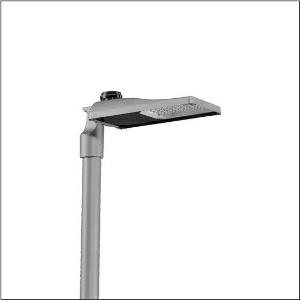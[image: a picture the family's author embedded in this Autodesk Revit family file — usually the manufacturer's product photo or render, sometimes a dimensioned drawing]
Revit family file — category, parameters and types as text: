
# Revit family: streetlight_sl_31_mini___st1_0a_5xh2d3bn08ha_f2e6
name_source: partatom
category: Lighting Fixtures
units: mm (PartAtom-declared; Revit-internal decimal feet)

## family parameters
Cut with Voids When Loaded = No
Host = Face
Light Source = No
Part Type = Normal
Room Calculation Point = No
Round Connector Dimension = Use Diameter
Shared = No

## types (1)
- --- (1 x LED, 9240 lm, 68.3 W, 3000K)
    Apparent Load = 68 VA
    CIE Flux Codes = 37 72 97 100 100
    Color Rendering = 70
    Color Temperature = 3000K
    Default Elevation = 1800 mm
    Description = Streetlight SL 31 mini NEMA (7pin) mast luminaire for post-top, side-entry; light control with lens of PMMA; light distribution: ST1.0a, direct asymmetric distribution, for standard-compliant lighting for roads and squares; LED: luminous flux: 9.240lm, light colour: 730, colour temperature: 3000K; luminous efficacy: 135,3lm/W; control: overheat protection, intelligent temperature release in ECG and LED module, constant luminous flux control, time-dependent luminous flux control, flexible luminous flux parameterisation, pre-setting: linear dimming characteristic; luminaire housing, of diecast aluminium, Siteco® metallic grey (DB 702S), corrosivity category C5 high according to DIN EN ISO 12944; cover of toughened safety glass, transparent, mast flange of diecast aluminium, Siteco® metallic grey (DB 702S), spigot size: 76/60mm, mast flange included unmounted; with cable H07RN-F 3x 1.5mm², cable length: 8,5m, connection cable pre-assembled; mains connection: 220..240V, AC, 50/60Hz; power consumption (at start of service life): 68,3W / (at end of service life): 74,8W / (with reduced operation 50%): 29,7W; protection rating (complete): IP66; insulation class (complete): insulation class I (protective earthing); impact resistance: IK10; certification: CE, ENEC, ENEC+, VDE, UKCA; permissible operating ambient temperature for outdoor applications: -40..+50°C; packaging unit: 1 piece

Light Distribution: ST1.0a
    Height = 76 mm
    Lamp = 1 x LED
    Lamp Light Flux = 9240 lm
    Lamp Power = 68.3 W
    Lamp count = 1
    Length = 547 mm
    Luminous efficacy = 135 lm/W
    Manufacturer = Siteco
    ModVariant = No
    Model = 5XH2D3BN08HA
    Number of Poles = 1
    OnlyDefault = Yes
    Power Factor = 1
    Product Name = Streetlight SL 31 mini | ST1.0a
    Product group = mast luminaire | pylon top
    ProductGroupID = 6100
    Protection Class = Protection class I
    Protection Degree = IP 66
    RLX_Detail_Level = 1
    RLX_Emergency_Light_Flux = 0 lm
    RLX_Emergency_Type = 0
    RLX_Emergency_Type_DB = No
    RlxData = <blob elided: 39961 chars, md5=201abd34>
    Socket = socket
    Standby Power = 0 W
    System Light Flux = 9240 lm
    System Power = 68 W
    Type Comments = factory setting: luminous flux: 100 % | dim-lin: 254 | 693 mA
    Type Image = l_1300322.jpg
    URL = http://relux.com
    VarID = @adj_054508
    Voltage = 0 V
    Weight = 0.00 kg
    Width = 265 mm

## geometry (parser evidence)
native form markers: Blend x4, Sweep x10
no freeform markers — native parametric forms only
